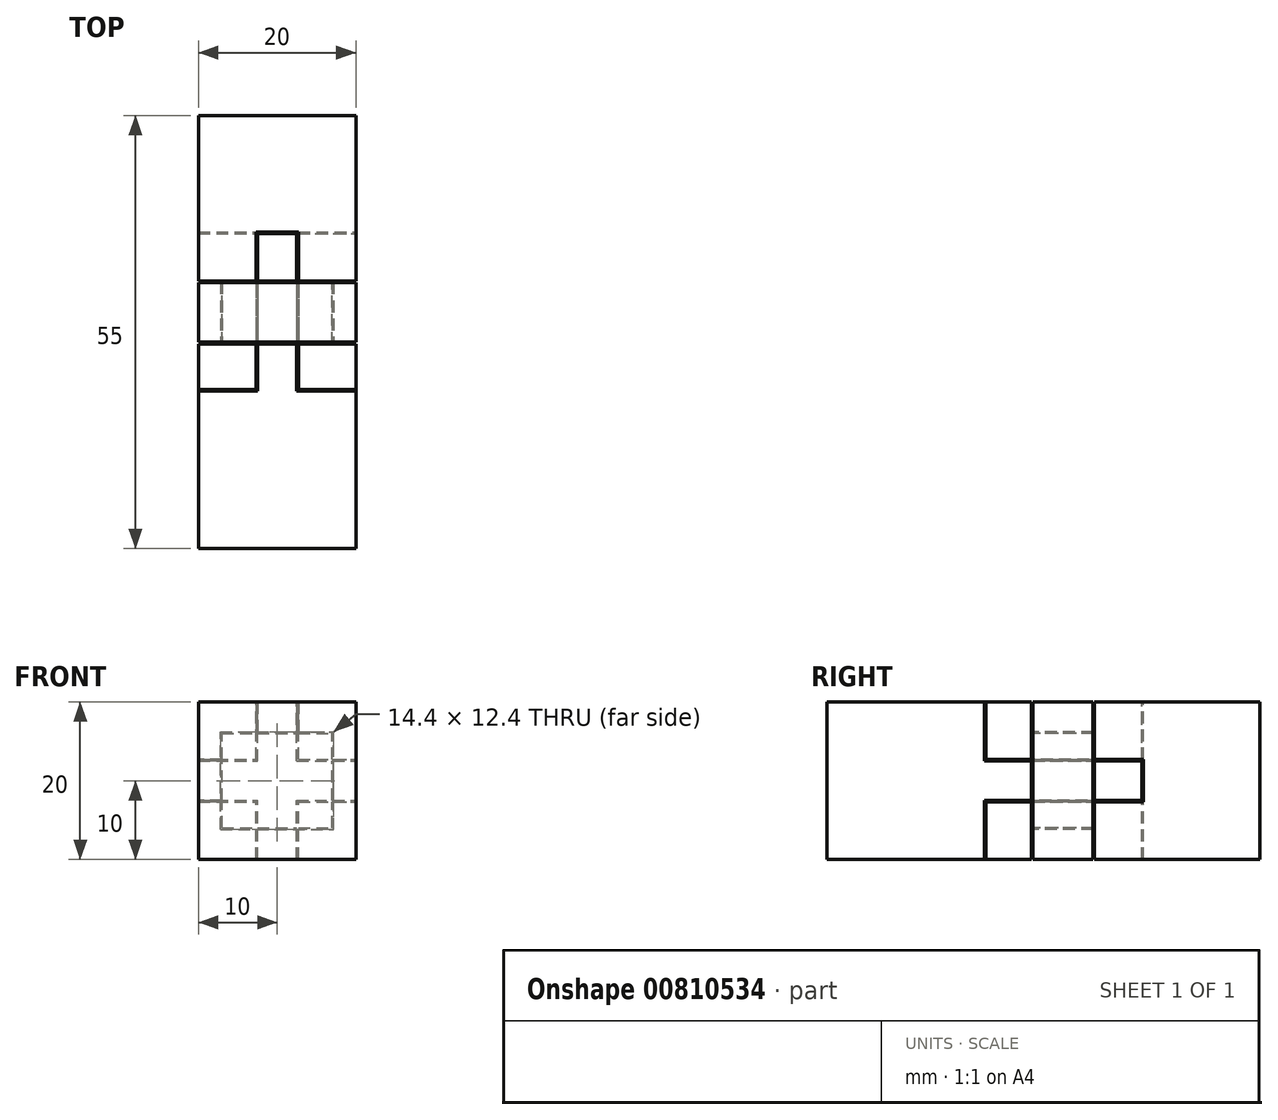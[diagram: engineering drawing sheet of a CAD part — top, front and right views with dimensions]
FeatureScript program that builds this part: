
annotation { "Feature Type Name" : "Feature", "Feature Type Description" : "" }
export const myFeature = defineFeature(function(context is Context, id is Id, definition is map)
    precondition{}
    {
        {
            var Q0;
            Q0=qCreatedBy(makeId("Front.planeOp"),FACE);
            var sketch = newSketch(context, id + "F0", { "sketchPlane" : qUnion([Q0])});
            skLineSegment(sketch, "E0.bottom", {"start": v(10, 10) * mm, "end": v(-10, 10) * mm});
            skLineSegment(sketch, "E0.top", {"start": v(10, -10) * mm, "end": v(-10, -10) * mm});
            skLineSegment(sketch, "E0.left", {"start": v(10, 10) * mm, "end": v(10, -10) * mm});
            skLineSegment(sketch, "E0.right", {"start": v(-10, 10) * mm, "end": v(-10, -10) * mm});
            skPoint(sketch, "E0.middle", {"position": v(0, 0) * mm});
            skSolve(sketch);
        }
        {
            var Q0;
            Q0=makeQuery(id+"F0.imprint","IMPRINT",FACE,{"disambiguationData":[TD([[makeQuery(id+"F0.imprint","IMPRINT",EDGE,{"derivedFrom":sQuery(id+"F0.wireOp",EDGE,"E0.bottom")}),1.0]])]});
            extrude(context, id + "F1", {"entities" : qUnion([Q0]), "depth" : 20 * mm, "offsetDistance" : 25 * mm});
        }
        {
            var Q0;
            Q0=makeQuery(id+"F1.opExtrude","CAP_FACE",FACE,{"disambiguationData":[OSD([sQuery(id+"F0.wireOp",EDGE,"E0.bottom"),sQuery(id+"F0.wireOp",EDGE,"E0.top"),sQuery(id+"F0.wireOp",EDGE,"E0.left"),sQuery(id+"F0.wireOp",EDGE,"E0.right")])],"isStart":true});
            var sketch = newSketch(context, id + "F2", { "sketchPlane" : qUnion([Q0])});
            skPoint(sketch, "E1.middle", {"position": v(0, 0) * mm});
            skLineSegment(sketch, "E2.bottom", {"start": v(-2.5, -10) * mm, "end": v(2.5, -10) * mm});
            skLineSegment(sketch, "E2.top", {"start": v(-2.5, 10) * mm, "end": v(2.5, 10) * mm});
            skLineSegment(sketch, "E2.left", {"start": v(-2.5, -10) * mm, "end": v(-2.5, 10) * mm});
            skLineSegment(sketch, "E2.right", {"start": v(2.5, -10) * mm, "end": v(2.5, 10) * mm});
            skPoint(sketch, "E3", {"position": v(0, -10) * mm});
            skLineSegment(sketch, "E4.bottom", {"start": v(10, 2.5) * mm, "end": v(-10, 2.5) * mm});
            skLineSegment(sketch, "E4.top", {"start": v(10, -2.5) * mm, "end": v(-10, -2.5) * mm});
            skLineSegment(sketch, "E4.left", {"start": v(10, 2.5) * mm, "end": v(10, -2.5) * mm});
            skLineSegment(sketch, "E4.right", {"start": v(-10, 2.5) * mm, "end": v(-10, -2.5) * mm});
            skSolve(sketch);
        }
        {
            var Q0;
            Q0=qSketchRegion(id+"F2",true);
            extrude(context, id + "F3", {"entities" : qUnion([Q0]), "operationType" : NewBodyOperationType.ADD, "depth" : 20 * mm, "offsetDistance" : 25 * mm});
        }
        {
            var Q0;
            Q0=qCreatedBy(makeId("Front.planeOp"),FACE);
            var sketch = newSketch(context, id + "F4", { "sketchPlane" : qUnion([Q0])});
            skPoint(sketch, "E5.middle", {"position": v(0, 0) * mm});
            skLineSegment(sketch, "E6.0", {"start": v(10, 10) * mm, "end": v(2, 10) * mm, "construction": true});
            skLineSegment(sketch, "E7.bottom", {"start": v(10, 10) * mm, "end": v(-10, 10) * mm});
            skLineSegment(sketch, "E7.top", {"start": v(10, -10) * mm, "end": v(-10, -10) * mm});
            skLineSegment(sketch, "E7.left", {"start": v(10, 10) * mm, "end": v(10, -10) * mm});
            skLineSegment(sketch, "E7.right", {"start": v(-10, 10) * mm, "end": v(-10, -10) * mm});
            skSolve(sketch);
        }
        {
            var Q0;
            Q0=qSketchRegion(id+"F4",true);
            extrude(context, id + "F5", {"entities" : qUnion([Q0]), "oppositeDirection" : true, "depth" : 35 * mm, "offsetDistance" : 25 * mm});
        }
        {
            var Q0;
            Q0=makeQuery(id+"F1.opExtrude","SWEPT_BODY",BODY,{"disambiguationData":[OSD([sQuery(id+"F0.wireOp",EDGE,"E0.bottom"),sQuery(id+"F0.wireOp",EDGE,"E0.top"),sQuery(id+"F0.wireOp",EDGE,"E0.left"),sQuery(id+"F0.wireOp",EDGE,"E0.right")])]});
            var Q1;
            Q1=makeQuery(id+"F5.opExtrude","SWEPT_BODY",BODY,{"disambiguationData":[OSD([sQuery(id+"F4.wireOp",EDGE,"E7.bottom"),sQuery(id+"F4.wireOp",EDGE,"E7.top"),sQuery(id+"F4.wireOp",EDGE,"E7.left"),sQuery(id+"F4.wireOp",EDGE,"E7.right")])]});
            booleanBodies(context, id + "F6", {"operationType" : BooleanOperationType.SUBTRACTION, "tools" : qUnion([Q0]), "targets" : qUnion([Q1]), "offset" : true, "offsetAll" : true, "offsetDistance" : 0.2 * mm, "keepTools" : true});
        }
        {
            var Q0;
            Q0=qCreatedBy(makeId("Right.planeOp"),FACE);
            var sketch = newSketch(context, id + "F7", { "sketchPlane" : qUnion([Q0])});
            skLineSegment(sketch, "E8.0", {"start": v(20, 10) * mm, "end": v(0, 10) * mm, "construction": true});
            skLineSegment(sketch, "E9.bottom", {"start": v(14, 14) * mm, "end": v(6, 14) * mm});
            skLineSegment(sketch, "E9.top", {"start": v(14, 6) * mm, "end": v(6, 6) * mm});
            skLineSegment(sketch, "E9.left", {"start": v(14, 14) * mm, "end": v(14, 6) * mm});
            skLineSegment(sketch, "E9.right", {"start": v(6, 14) * mm, "end": v(6, 6) * mm});
            skPoint(sketch, "E9.middle", {"position": v(10, 10) * mm});
            skLineSegment(sketch, "E10", {"start": v(18.1, 0) * mm, "end": v(163.16, 0) * mm, "construction": true});
            skLineSegment(sketch, "E11.MirrorCS", {"start": v(14, -14) * mm, "end": v(14, -6) * mm});
            skLineSegment(sketch, "E12.MirrorCS", {"start": v(14, -14) * mm, "end": v(6, -14) * mm});
            skLineSegment(sketch, "E13.MirrorCS", {"start": v(6, -14) * mm, "end": v(6, -6) * mm});
            skLineSegment(sketch, "E14.MirrorCS", {"start": v(14, -6) * mm, "end": v(6, -6) * mm});
            skSolve(sketch);
        }
        {
            var Q0;
            Q0 = qSketchRegion(id + "F7", true);
            extrude(context, id + "F8", {"entities" : qUnion([Q0]), "operationType" : NewBodyOperationType.REMOVE, "endBound" : BoundingType.SYMMETRIC, "oppositeDirection" : true, "depth" : 100 * mm, "offsetDistance" : 25 * mm});
        }
        {
            var Q0;
            Q0=qCreatedBy(makeId("Top.planeOp"),FACE);
            var sketch = newSketch(context, id + "F9", { "sketchPlane" : qUnion([Q0])});
            skLineSegment(sketch, "E15.0", {"start": v(-10, 6) * mm, "end": v(-10, 14) * mm, "construction": true});
            skLineSegment(sketch, "E16.bottom", {"start": v(-10, 14) * mm, "end": v(-7, 14) * mm});
            skLineSegment(sketch, "E16.top", {"start": v(-10, 6) * mm, "end": v(-7, 6) * mm});
            skLineSegment(sketch, "E16.left", {"start": v(-10, 14) * mm, "end": v(-10, 6) * mm});
            skLineSegment(sketch, "E16.right", {"start": v(-7, 14) * mm, "end": v(-7, 6) * mm});
            skLineSegment(sketch, "E17", {"start": v(0, 55.7) * mm, "end": v(0, -234.44) * mm, "construction": true});
            skLineSegment(sketch, "E18.MirrorCS", {"start": v(10, 14) * mm, "end": v(10, 6) * mm});
            skLineSegment(sketch, "E19.MirrorCS", {"start": v(10, 6) * mm, "end": v(7, 6) * mm});
            skLineSegment(sketch, "E20.MirrorCS", {"start": v(10, 6) * mm, "end": v(10, 14) * mm, "construction": true});
            skLineSegment(sketch, "E21.MirrorCS", {"start": v(10, 14) * mm, "end": v(7, 14) * mm});
            skLineSegment(sketch, "E22.MirrorCS", {"start": v(7, 14) * mm, "end": v(7, 6) * mm});
            skSolve(sketch);
        }
        {
            var Q0;
            Q0 = qSketchRegion(id + "F9", true);
            extrude(context, id + "F10", {"entities" : qUnion([Q0]), "operationType" : NewBodyOperationType.REMOVE, "endBound" : BoundingType.SYMMETRIC, "oppositeDirection" : true, "depth" : 100 * mm, "offsetDistance" : 25 * mm});
        }
        {
            var Q0;
            Q0=qCreatedBy(makeId("Front.planeOp"),FACE);
            var Q1;
            {var subQ0=sQuery(id+"F2.wireOp",EDGE,"E4.bottom");Q1=makeQuery(id+"F10.boolean.opBoolean","INTERSECT",VERTEX,{"derivedFrom":[makeQuery(id+"F6.tempBoolean.opBoolean","COPY",FACE,{"derivedFrom":makeQuery(id+"F6.offsetTempBody.opPattern","COPY",FACE,{"derivedFrom":makeQuery(id+"F3.opExtrude","SWEPT_FACE",FACE,{"disambiguationData":[OSD([subQ0]),TDD([makeQuery(id+"F2.imprint","IMPRINT",EDGE,{"disambiguationData":[TD([[makeQuery(id+"F2.imprint","INTERSECT",VERTEX,{"derivedFrom":[sQuery(id+"F2.wireOp",EDGE,"E2.left"),subQ0]}),-1.0]])],"derivedFrom":subQ0})])]}),"instanceName":"1"})}),makeQuery(id+"F10.opExtrude","SWEPT_FACE",FACE,{"disambiguationData":[OSD([sQuery(id+"F9.wireOp",EDGE,"E19.MirrorCS")])]}),makeQuery(id+"F10.opExtrude","SWEPT_FACE",FACE,{"disambiguationData":[OSD([sQuery(id+"F9.wireOp",EDGE,"E22.MirrorCS")])]})]});}
            cPlane(context, id + "F11", {"entities" : qUnion([Q0, Q1]), "cplaneType" : CPlaneType.PLANE_POINT, "offset" : 25 * mm, "width" : 150 * mm, "height" : 150 * mm});
        }
        {
            var Q0;
            Q0=qCreatedBy(id+"F11.planeOp",FACE);
            var sketch = newSketch(context, id + "F12", { "sketchPlane" : qUnion([Q0])});
            skPoint(sketch, "E23.0", {"position": v(0, 0) * mm});
            skLineSegment(sketch, "E24.0", {"start": v(10, -2.5) * mm, "end": v(10, 2.5) * mm, "construction": true});
            skLineSegment(sketch, "E25.0", {"start": v(2.5, 10) * mm, "end": v(-2.5, 10) * mm, "construction": true});
            skLineSegment(sketch, "E26.bottom", {"start": v(10, 10) * mm, "end": v(-10, 10) * mm});
            skLineSegment(sketch, "E26.top", {"start": v(10, -10) * mm, "end": v(-10, -10) * mm});
            skLineSegment(sketch, "E26.left", {"start": v(10, 10) * mm, "end": v(10, -10) * mm});
            skLineSegment(sketch, "E26.right", {"start": v(-10, 10) * mm, "end": v(-10, -10) * mm});
            skSolve(sketch);
        }
        {
            var Q0;
            Q0 = qSketchRegion(id + "F12", true);
            var Q1;
            Q1=makeQuery(id+"F10.boolean.opBoolean","MERGE",FACE,{"derivedFrom":[makeQuery(id+"F8.boolean.opBoolean","COPY",FACE,{"disambiguationData":[TD([makeQuery(id+"F5.opExtrude","SWEPT_FACE",FACE,{"disambiguationData":[OSD([sQuery(id+"F4.wireOp",EDGE,"E7.left")])]})])],"derivedFrom":makeQuery(id+"F8.opExtrude","SWEPT_FACE",FACE,{"disambiguationData":[OSD([sQuery(id+"F7.wireOp",EDGE,"E9.left")])]})}),makeQuery(id+"F10.opExtrude","SWEPT_FACE",FACE,{"disambiguationData":[OSD([sQuery(id+"F9.wireOp",EDGE,"E21.MirrorCS")])]})]});
            extrude(context, id + "F13", {"entities" : qUnion([Q0]), "endBound" : BoundingType.UP_TO_SURFACE, "oppositeDirection" : true, "depth" : 25 * mm, "endBoundEntityFace" : qUnion([Q1]), "offsetDistance" : 25 * mm});
        }
        {
            var Q0;
            Q0=makeQuery(id+"F1.opExtrude","SWEPT_BODY",BODY,{"disambiguationData":[OSD([sQuery(id+"F0.wireOp",EDGE,"E0.bottom"),sQuery(id+"F0.wireOp",EDGE,"E0.top"),sQuery(id+"F0.wireOp",EDGE,"E0.left"),sQuery(id+"F0.wireOp",EDGE,"E0.right")])]});
            var Q1;
            Q1=makeQuery(id+"F5.opExtrude","SWEPT_BODY",BODY,{"disambiguationData":[OSD([sQuery(id+"F4.wireOp",EDGE,"E7.bottom"),sQuery(id+"F4.wireOp",EDGE,"E7.top"),sQuery(id+"F4.wireOp",EDGE,"E7.left"),sQuery(id+"F4.wireOp",EDGE,"E7.right")])]});
            var Q2;
            Q2=makeQuery(id+"F13.opExtrude","SWEPT_BODY",BODY,{"disambiguationData":[OSD([sQuery(id+"F12.wireOp",EDGE,"E26.bottom"),sQuery(id+"F12.wireOp",EDGE,"E26.top"),sQuery(id+"F12.wireOp",EDGE,"E26.left"),sQuery(id+"F12.wireOp",EDGE,"E26.right")])]});
            booleanBodies(context, id + "F14", {"operationType" : BooleanOperationType.SUBTRACTION, "tools" : qUnion([Q0, Q1]), "targets" : qUnion([Q2]), "offset" : true, "offsetAll" : true, "offsetDistance" : 0.2 * mm, "keepTools" : true});
        }
    });
